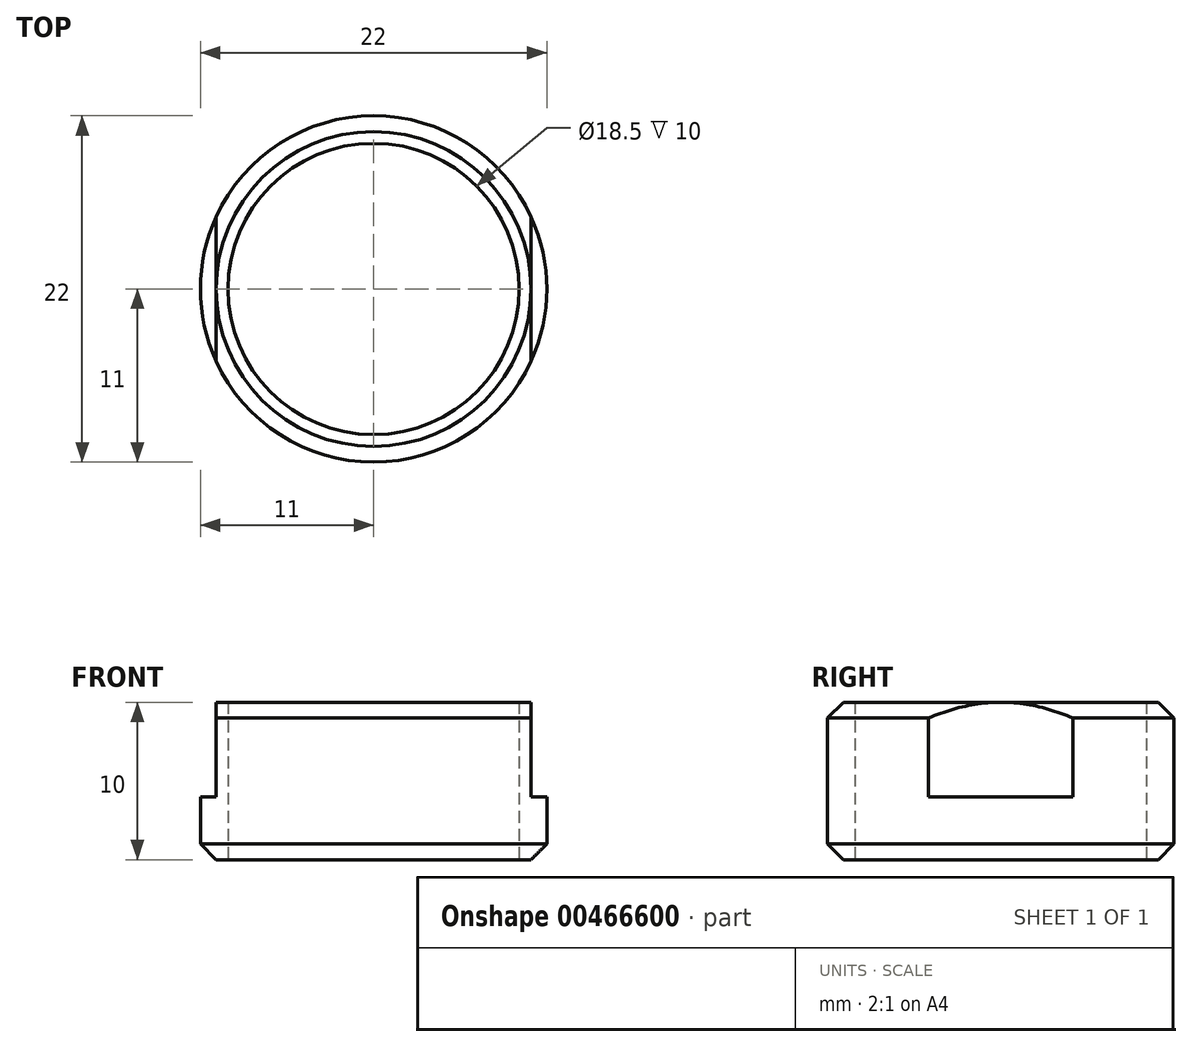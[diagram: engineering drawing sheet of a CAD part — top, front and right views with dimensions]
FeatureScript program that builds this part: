
annotation { "Feature Type Name" : "Feature", "Feature Type Description" : "" }
export const myFeature = defineFeature(function(context is Context, id is Id, definition is map)
    precondition{}
    {
        {
            var Q0;
            Q0=qCreatedBy(makeId("Top.planeOp"),FACE);
            var sketch = newSketch(context, id + "F0", { "sketchPlane" : qUnion([Q0])});
            skCircle(sketch, "E0", {"center": v(0, 0) * mm, "radius": 11 * mm});
            skCircle(sketch, "E1", {"center": v(0, 0) * mm, "radius": 9.25 * mm});
            skSolve(sketch);
        }
        {
            var Q0;
            Q0=makeQuery(id+"F0.imprint","IMPRINT",FACE,{"disambiguationData":[TD([[makeQuery(id+"F0.imprint","IMPRINT",EDGE,{"derivedFrom":sQuery(id+"F0.wireOp",EDGE,"E0")}),1.0]])]});
            extrude(context, id + "F1", {"entities" : qUnion([Q0]), "depth" : 10 * mm, "offsetDistance" : 25 * mm});
        }
        {
            var Q0;
            Q0=makeQuery(id+"F1.opExtrude","CAP_FACE",FACE,{"disambiguationData":[OSD([sQuery(id+"F0.wireOp",EDGE,"E0"),sQuery(id+"F0.wireOp",EDGE,"E1")])],"isStart":false});
            var sketch = newSketch(context, id + "F2", { "sketchPlane" : qUnion([Q0])});
            skLineSegment(sketch, "E2.bottom", {"start": v(-10, 26.99) * mm, "end": v(10, 26.99) * mm});
            skLineSegment(sketch, "E2.top", {"start": v(-10, -26.99) * mm, "end": v(10, -26.99) * mm});
            skLineSegment(sketch, "E2.left", {"start": v(-10, 26.99) * mm, "end": v(-10, -26.99) * mm});
            skLineSegment(sketch, "E2.right", {"start": v(10, 26.99) * mm, "end": v(10, -26.99) * mm});
            skPoint(sketch, "E2.middle", {"position": v(0, 0) * mm});
            skSolve(sketch);
        }
        {
            var Q0;
            {var subQ0=sQuery(id+"F2.wireOp",EDGE,"E2.left");var subQ1=makeQuery(id+"F1.opExtrude","CAP_EDGE",EDGE,{"disambiguationData":[OSD([sQuery(id+"F0.wireOp",EDGE,"E0")])],"isStart":false});var subQ2=makeQuery(id+"F2.imprint","INTERSECT",VERTEX,{"disambiguationData":[OD(0.0)],"derivedFrom":[subQ1,subQ0]});Q0=makeQuery(id+"F2.imprint","IMPRINT",FACE,{"disambiguationData":[TD([[makeQuery(id+"F2.imprint","IMPRINT",EDGE,{"disambiguationData":[TD([[subQ2,-1.0]])],"derivedFrom":subQ0}),-1.0]])]});}
            var Q1;
            {var subQ0=sQuery(id+"F2.wireOp",EDGE,"E2.right");var subQ1=makeQuery(id+"F1.opExtrude","CAP_EDGE",EDGE,{"disambiguationData":[OSD([sQuery(id+"F0.wireOp",EDGE,"E0")])],"isStart":false});var subQ2=makeQuery(id+"F2.imprint","INTERSECT",VERTEX,{"disambiguationData":[OD(0.0)],"derivedFrom":[subQ1,subQ0]});Q1=makeQuery(id+"F2.imprint","IMPRINT",FACE,{"disambiguationData":[TD([[makeQuery(id+"F2.imprint","IMPRINT",EDGE,{"disambiguationData":[TD([[subQ2,-1.0]])],"derivedFrom":subQ0}),1.0]])]});}
            extrude(context, id + "F3", {"entities" : qUnion([Q0, Q1]), "operationType" : NewBodyOperationType.REMOVE, "oppositeDirection" : true, "depth" : 6 * mm, "offsetDistance" : 25 * mm});
        }
        {
            var Q0;
            Q0=makeQuery(id+"F1.opExtrude","CAP_EDGE",EDGE,{"disambiguationData":[OSD([sQuery(id+"F0.wireOp",EDGE,"E0")])],"isStart":true});
            var Q1;
            Q1=makeQuery(id+"F3.boolean.opBoolean","SPLIT",EDGE,{"disambiguationData":[OD(1.0)],"derivedFrom":makeQuery(id+"F1.opExtrude","CAP_EDGE",EDGE,{"disambiguationData":[OSD([sQuery(id+"F0.wireOp",EDGE,"E0")])],"isStart":false})});
            var Q2;
            Q2=makeQuery(id+"F3.boolean.opBoolean","SPLIT",EDGE,{"disambiguationData":[OD(0.0)],"derivedFrom":makeQuery(id+"F1.opExtrude","CAP_EDGE",EDGE,{"disambiguationData":[OSD([sQuery(id+"F0.wireOp",EDGE,"E0")])],"isStart":false})});
            chamfer(context, id + "F4", {"entities" : qUnion([Q0, Q1, Q2]), "width" : 1 * mm, "tangentPropagation" : true});
        }
    });
